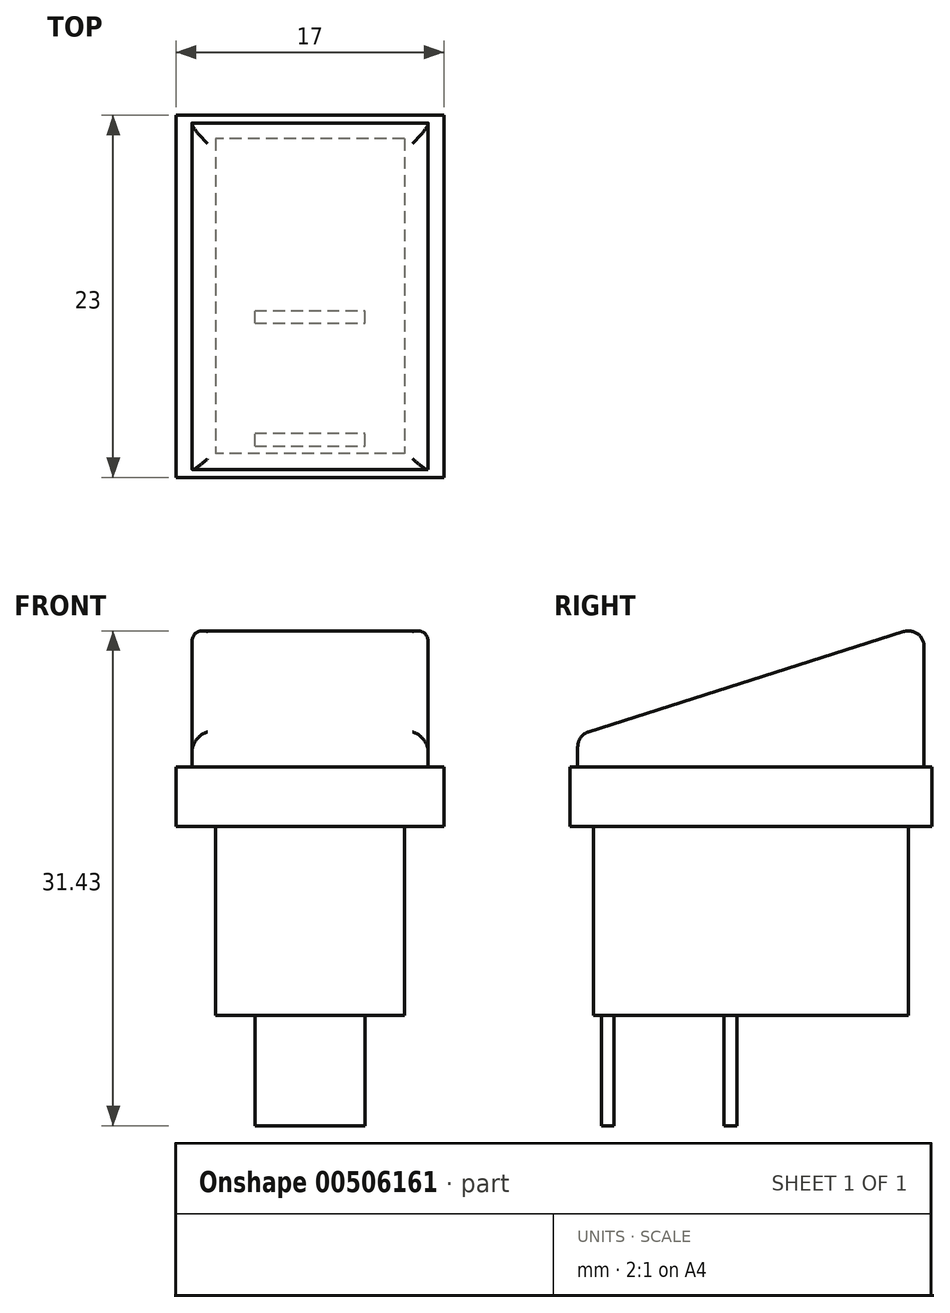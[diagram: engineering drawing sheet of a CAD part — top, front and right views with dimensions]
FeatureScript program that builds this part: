
annotation { "Feature Type Name" : "Feature", "Feature Type Description" : "" }
export const myFeature = defineFeature(function(context is Context, id is Id, definition is map)
    precondition{}
    {
        {
            var Q0;
            Q0=qCreatedBy(makeId("Top.planeOp"),FACE);
            var sketch = newSketch(context, id + "F0", { "sketchPlane" : qUnion([Q0])});
            skLineSegment(sketch, "E0.bottom", {"start": v(6, 10) * mm, "end": v(-6, 10) * mm});
            skLineSegment(sketch, "E0.top", {"start": v(6, -10) * mm, "end": v(-6, -10) * mm});
            skLineSegment(sketch, "E0.left", {"start": v(6, 10) * mm, "end": v(6, -10) * mm});
            skLineSegment(sketch, "E0.right", {"start": v(-6, 10) * mm, "end": v(-6, -10) * mm});
            skPoint(sketch, "E0.middle", {"position": v(0, 0) * mm});
            skSolve(sketch);
        }
        {
            var Q0;
            Q0=makeQuery(id+"F0.imprint","IMPRINT",FACE,{"disambiguationData":[TD([[makeQuery(id+"F0.imprint","IMPRINT",EDGE,{"derivedFrom":sQuery(id+"F0.wireOp",EDGE,"E0.bottom")}),1.0]])]});
            extrude(context, id + "F1", {"entities" : qUnion([Q0]), "depth" : 12 * mm});
        }
        {
            var Q0;
            Q0=makeQuery(id+"F1.opExtrude","CAP_FACE",FACE,{"disambiguationData":[OSD([sQuery(id+"F0.wireOp",EDGE,"E0.bottom"),sQuery(id+"F0.wireOp",EDGE,"E0.top"),sQuery(id+"F0.wireOp",EDGE,"E0.left"),sQuery(id+"F0.wireOp",EDGE,"E0.right")])],"isStart":false});
            var sketch = newSketch(context, id + "F2", { "sketchPlane" : qUnion([Q0])});
            skLineSegment(sketch, "E1.bottom", {"start": v(8.5, 11.5) * mm, "end": v(-8.5, 11.5) * mm});
            skLineSegment(sketch, "E1.top", {"start": v(8.5, -11.5) * mm, "end": v(-8.5, -11.5) * mm});
            skLineSegment(sketch, "E1.left", {"start": v(8.5, 11.5) * mm, "end": v(8.5, -11.5) * mm});
            skLineSegment(sketch, "E1.right", {"start": v(-8.5, 11.5) * mm, "end": v(-8.5, -11.5) * mm});
            skPoint(sketch, "E1.middle", {"position": v(0, 0) * mm});
            skSolve(sketch);
        }
        {
            var Q0;
            Q0=makeQuery(id+"F2.imprint","IMPRINT",FACE,{"disambiguationData":[TD([[makeQuery(id+"F2.imprint","IMPRINT",EDGE,{"derivedFrom":sQuery(id+"F2.wireOp",EDGE,"E1.bottom")}),1.0]])]});
            var Q1;
            Q1=makeQuery(id+"F2.imprint","IMPRINT",FACE,{"disambiguationData":[TD([[makeQuery(id+"F2.imprint","IMPRINT",EDGE,{"derivedFrom":makeQuery(id+"F1.opExtrude","CAP_EDGE",EDGE,{"disambiguationData":[OSD([sQuery(id+"F0.wireOp",EDGE,"E0.bottom")])],"isStart":false})}),1.0]])]});
            extrude(context, id + "F3", {"entities" : qUnion([Q0, Q1]), "operationType" : NewBodyOperationType.ADD, "depth" : 3.8 * mm});
        }
        {
            var Q0;
            Q0=makeQuery(id+"F1.opExtrude","CAP_FACE",FACE,{"disambiguationData":[OSD([sQuery(id+"F0.wireOp",EDGE,"E0.bottom"),sQuery(id+"F0.wireOp",EDGE,"E0.top"),sQuery(id+"F0.wireOp",EDGE,"E0.left"),sQuery(id+"F0.wireOp",EDGE,"E0.right")])],"isStart":true});
            var sketch = newSketch(context, id + "F4", { "sketchPlane" : qUnion([Q0])});
            skLineSegment(sketch, "E2.bottom", {"start": v(-3.5, 9.5) * mm, "end": v(3.5, 9.5) * mm});
            skLineSegment(sketch, "E2.top", {"start": v(-3.5, 8.7) * mm, "end": v(3.5, 8.7) * mm});
            skLineSegment(sketch, "E2.left", {"start": v(-3.5, 9.5) * mm, "end": v(-3.5, 8.7) * mm});
            skLineSegment(sketch, "E2.right", {"start": v(3.5, 9.5) * mm, "end": v(3.5, 8.7) * mm});
            skLineSegment(sketch, "E3.bottom", {"start": v(-3.5, 1.7) * mm, "end": v(3.5, 1.7) * mm});
            skLineSegment(sketch, "E3.top", {"start": v(-3.5, 0.9) * mm, "end": v(3.5, 0.9) * mm});
            skLineSegment(sketch, "E3.left", {"start": v(-3.5, 1.7) * mm, "end": v(-3.5, 0.9) * mm});
            skLineSegment(sketch, "E3.right", {"start": v(3.5, 1.7) * mm, "end": v(3.5, 0.9) * mm});
            skSolve(sketch);
        }
        {
            var Q0;
            Q0=makeQuery(id+"F4.imprint","IMPRINT",FACE,{"disambiguationData":[TD([[makeQuery(id+"F4.imprint","IMPRINT",EDGE,{"derivedFrom":sQuery(id+"F4.wireOp",EDGE,"E2.bottom")}),-1.0]])]});
            var Q1;
            Q1=makeQuery(id+"F4.imprint","IMPRINT",FACE,{"disambiguationData":[TD([[makeQuery(id+"F4.imprint","IMPRINT",EDGE,{"derivedFrom":sQuery(id+"F4.wireOp",EDGE,"E3.bottom")}),-1.0]])]});
            extrude(context, id + "F5", {"entities" : qUnion([Q0, Q1]), "operationType" : NewBodyOperationType.ADD, "depth" : 7 * mm});
        }
        {
            var Q0;
            Q0=qCreatedBy(makeId("Right.planeOp"),FACE);
            var sketch = newSketch(context, id + "F6", { "sketchPlane" : qUnion([Q0])});
            skLineSegment(sketch, "E4.0", {"start": v(11.5, 15.8) * mm, "end": v(-11.5, 15.8) * mm});
            skLineSegment(sketch, "E5", {"start": v(-11, 15.8) * mm, "end": v(-11, 17.8) * mm});
            skLineSegment(sketch, "E6", {"start": v(-11, 17.8) * mm, "end": v(11, 24.8) * mm});
            skLineSegment(sketch, "E7", {"start": v(11, 24.8) * mm, "end": v(11, 15.8) * mm});
            skSolve(sketch);
        }
        {
            var Q0;
            {var subQ0=sQuery(id+"F6.wireOp",EDGE,"E5");Q0=makeQuery(id+"F6.imprint","IMPRINT",FACE,{"disambiguationData":[TD([[makeQuery(id+"F6.imprint","IMPRINT",EDGE,{"derivedFrom":subQ0}),-1.0]])]});}
            extrude(context, id + "F7", {"entities" : qUnion([Q0]), "operationType" : NewBodyOperationType.ADD, "endBound" : BoundingType.SYMMETRIC, "depth" : 15 * mm});
        }
        {
            var Q0;
            Q0=makeQuery(id+"F7.opExtrude","SWEPT_FACE",FACE,{"disambiguationData":[OSD([sQuery(id+"F6.wireOp",EDGE,"E6")])]});
            fillet(context, id + "F8", {"entities" : qUnion([Q0]), "radius" : 1 * mm, "tangentPropagation" : true, "allowEdgeOverflow" : false});
        }
    });
